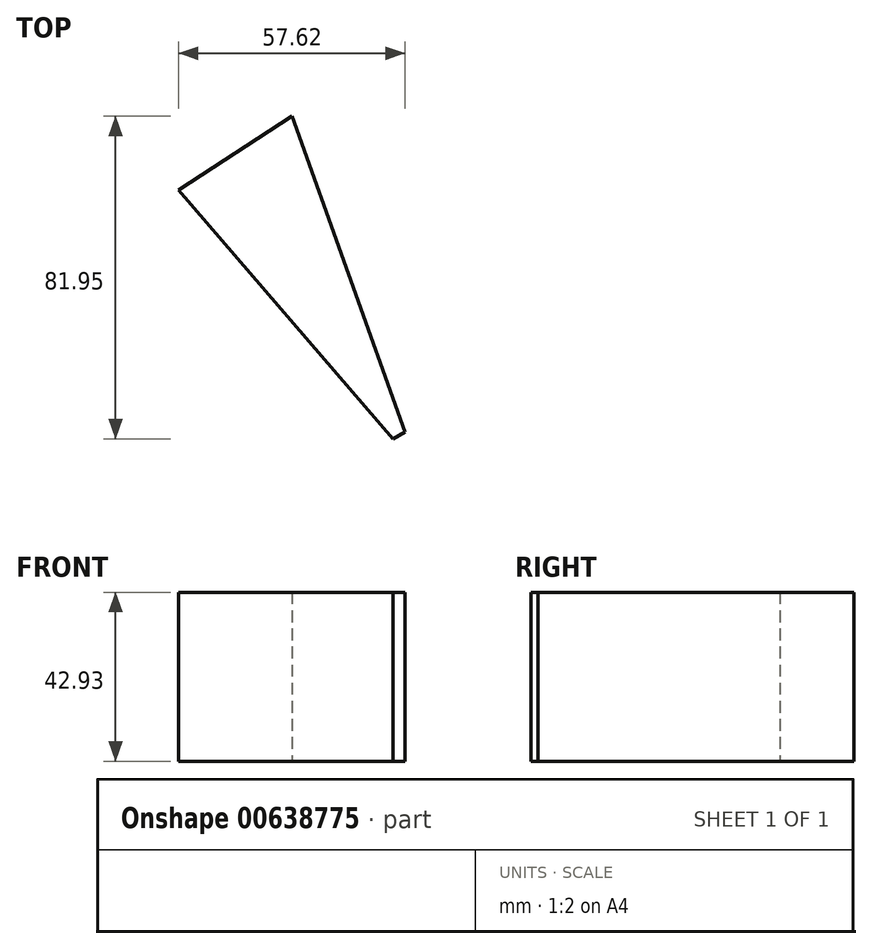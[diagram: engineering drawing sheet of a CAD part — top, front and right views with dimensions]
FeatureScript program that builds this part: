
annotation { "Feature Type Name" : "Feature", "Feature Type Description" : "" }
export const myFeature = defineFeature(function(context is Context, id is Id, definition is map)
    precondition{}
    {
        {
            var Q0;
            Q0=qCreatedBy(makeId("Top.planeOp"),FACE);
            var sketch = newSketch(context, id + "F0", { "sketchPlane" : qUnion([Q0])});
            skLineSegment(sketch, "E0", {"start": v(-36, 20.9) * mm, "end": v(18.52, -42.33) * mm});
            skLineSegment(sketch, "E1", {"start": v(21.6, -40.55) * mm, "end": v(-7.17, 39.62) * mm});
            skLineSegment(sketch, "E2", {"start": v(-36, 20.9) * mm, "end": v(-7.17, 39.62) * mm});
            skLineSegment(sketch, "E3", {"start": v(18.52, -42.33) * mm, "end": v(21.6, -40.55) * mm});
            skSolve(sketch);
        }
        {
            var Q0;
            Q0=makeQuery(id+"F0.imprint","IMPRINT",FACE,{"disambiguationData":[TD([[makeQuery(id+"F0.imprint","IMPRINT",EDGE,{"derivedFrom":sQuery(id+"F0.wireOp",EDGE,"E0")}),1.0]])]});
            extrude(context, id + "F1", {"entities" : qUnion([Q0]), "depth" : 41.15 * mm, "offsetDistance" : 25.4 * mm, "hasSecondDirection" : true, "secondDirectionOppositeDirection" : true, "secondDirectionDepth" : 1.78 * mm});
        }
    });
